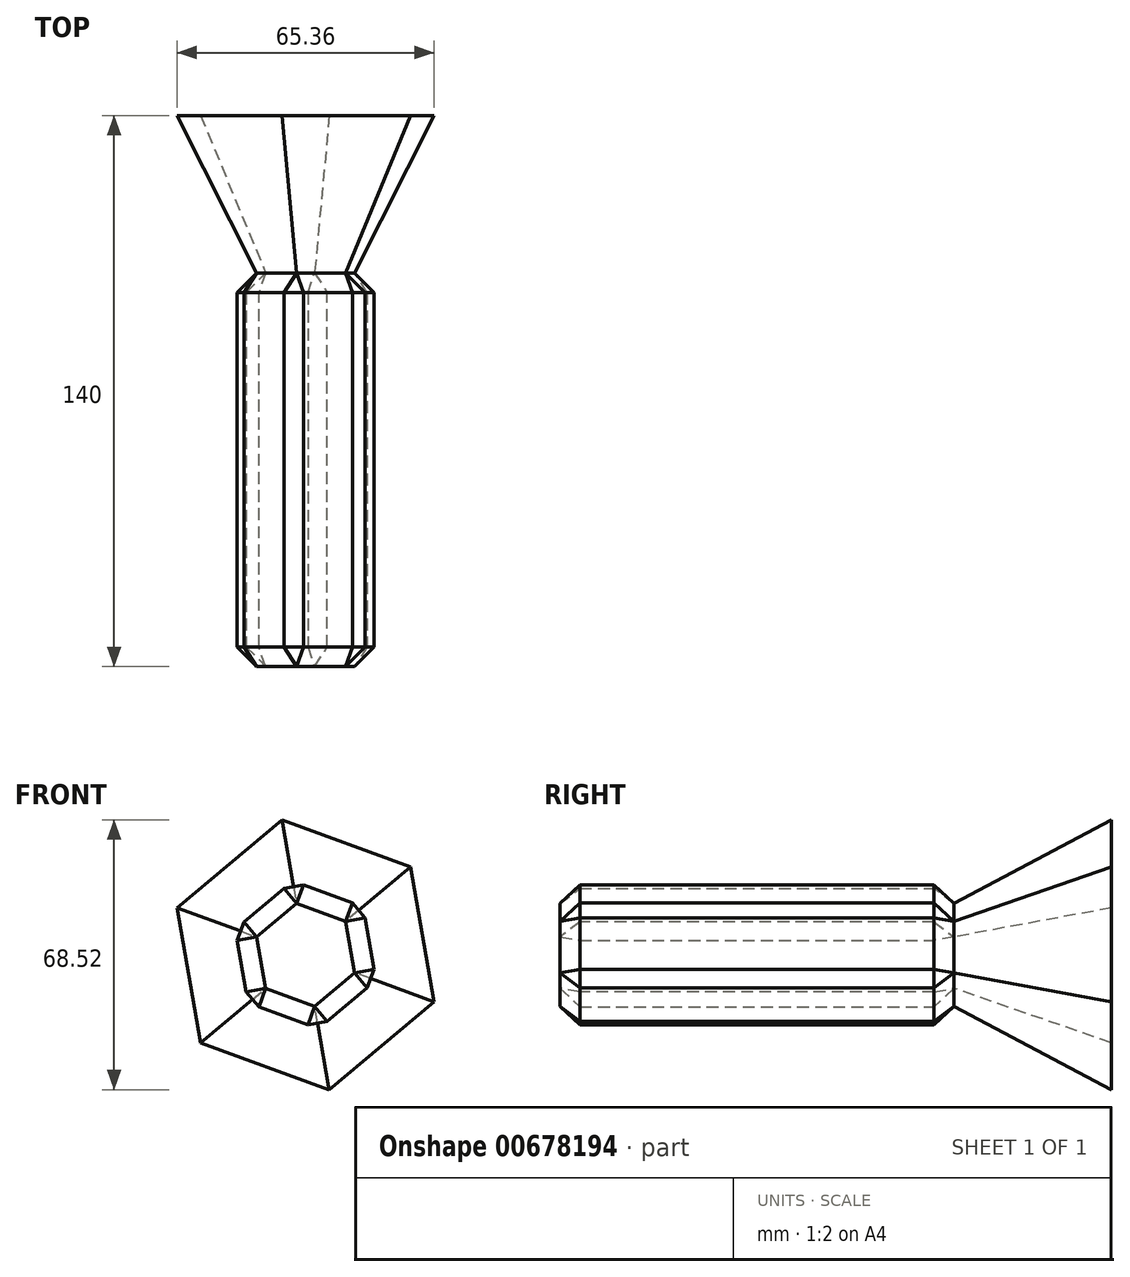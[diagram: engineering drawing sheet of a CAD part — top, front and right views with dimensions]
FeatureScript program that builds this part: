
annotation { "Feature Type Name" : "Feature", "Feature Type Description" : "" }
export const myFeature = defineFeature(function(context is Context, id is Id, definition is map)
    precondition{}
    {
        {
            var Q0;
            Q0=qCreatedBy(makeId("Front.planeOp"),FACE);
            var sketch = newSketch(context, id + "F0", { "sketchPlane" : qUnion([Q0])});
            skLineSegment(sketch, "E0.0", {"start": v(17.87, -6.51) * mm, "end": v(3.3, -18.73) * mm});
            skLineSegment(sketch, "E0.1", {"start": v(3.3, -18.73) * mm, "end": v(-14.58, -12.22) * mm});
            skLineSegment(sketch, "E0.2", {"start": v(-14.58, -12.22) * mm, "end": v(-17.87, 6.51) * mm});
            skLineSegment(sketch, "E0.3", {"start": v(-17.87, 6.51) * mm, "end": v(-3.3, 18.73) * mm});
            skLineSegment(sketch, "E0.4", {"start": v(-3.3, 18.73) * mm, "end": v(14.58, 12.22) * mm});
            skLineSegment(sketch, "E0.5", {"start": v(14.58, 12.22) * mm, "end": v(17.87, -6.51) * mm});
            skSolve(sketch);
        }
        {
            var Q0;
            Q0=makeQuery(id+"F0.imprint","IMPRINT",FACE,{"disambiguationData":[TD([[makeQuery(id+"F0.imprint","IMPRINT",EDGE,{"derivedFrom":sQuery(id+"F0.wireOp",EDGE,"E0.0")}),-1.0]])]});
            var Q1;
            Q1=sQuery(id+"F0.wireOp",EDGE,"E0.0");
            var Q2;
            Q2=sQuery(id+"F0.wireOp",EDGE,"E0.1");
            var Q3;
            Q3=sQuery(id+"F0.wireOp",EDGE,"E0.2");
            var Q4;
            Q4=sQuery(id+"F0.wireOp",EDGE,"E0.4");
            var Q5;
            Q5=sQuery(id+"F0.wireOp",EDGE,"E0.5");
            var Q6;
            Q6=sQuery(id+"F0.wireOp",EDGE,"E0.3");
            extrude(context, id + "F1", {"entities" : qUnion([Q0]), "surfaceEntities" : qUnion([Q1, Q2, Q3, Q4, Q5, Q6]), "depth" : 100 * mm, "offsetDistance" : 25 * mm});
        }
        {
            var Q0;
            Q0=makeQuery(id+"F1.opExtrude","CAP_FACE",FACE,{"disambiguationData":[OSD([sQuery(id+"F0.wireOp",EDGE,"E0.0"),sQuery(id+"F0.wireOp",EDGE,"E0.1"),sQuery(id+"F0.wireOp",EDGE,"E0.2"),sQuery(id+"F0.wireOp",EDGE,"E0.3"),sQuery(id+"F0.wireOp",EDGE,"E0.4"),sQuery(id+"F0.wireOp",EDGE,"E0.5")])],"isStart":false});
            var Q1;
            Q1=makeQuery(id+"F1.opExtrude","CAP_FACE",FACE,{"disambiguationData":[OSD([sQuery(id+"F0.wireOp",EDGE,"E0.0"),sQuery(id+"F0.wireOp",EDGE,"E0.1"),sQuery(id+"F0.wireOp",EDGE,"E0.2"),sQuery(id+"F0.wireOp",EDGE,"E0.3"),sQuery(id+"F0.wireOp",EDGE,"E0.4"),sQuery(id+"F0.wireOp",EDGE,"E0.5")])],"isStart":true});
            var Q2;
            Q2=makeQuery(id+"F1.opExtrude","SWEPT_FACE",FACE,{"disambiguationData":[OSD([sQuery(id+"F0.wireOp",EDGE,"E0.4")])]});
            var Q3;
            Q3=makeQuery(id+"F1.opExtrude","SWEPT_FACE",FACE,{"disambiguationData":[OSD([sQuery(id+"F0.wireOp",EDGE,"E0.5")])]});
            var Q4;
            Q4=makeQuery(id+"F1.opExtrude","SWEPT_FACE",FACE,{"disambiguationData":[OSD([sQuery(id+"F0.wireOp",EDGE,"E0.0")])]});
            var Q5;
            Q5=makeQuery(id+"F1.opExtrude","SWEPT_FACE",FACE,{"disambiguationData":[OSD([sQuery(id+"F0.wireOp",EDGE,"E0.1")])]});
            var Q6;
            Q6=makeQuery(id+"F1.opExtrude","SWEPT_FACE",FACE,{"disambiguationData":[OSD([sQuery(id+"F0.wireOp",EDGE,"E0.2")])]});
            chamfer(context, id + "F2", {"entities" : qUnion([Q0, Q1, Q2, Q3, Q4, Q5, Q6]), "width" : 5 * mm, "tangentPropagation" : true});
        }
        {
            var Q0;
            Q0=makeQuery(id+"F1.opExtrude","CAP_FACE",FACE,{"disambiguationData":[OSD([sQuery(id+"F0.wireOp",EDGE,"E0.0"),sQuery(id+"F0.wireOp",EDGE,"E0.1"),sQuery(id+"F0.wireOp",EDGE,"E0.2"),sQuery(id+"F0.wireOp",EDGE,"E0.3"),sQuery(id+"F0.wireOp",EDGE,"E0.4"),sQuery(id+"F0.wireOp",EDGE,"E0.5")])],"isStart":true});
            extrude(context, id + "F3", {"entities" : qUnion([Q0]), "operationType" : NewBodyOperationType.ADD, "depth" : 40 * mm, "offsetDistance" : 25 * mm, "hasDraft" : true, "draftAngle" : 25 * degree});
        }
    });
